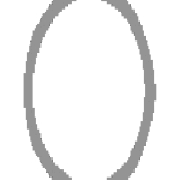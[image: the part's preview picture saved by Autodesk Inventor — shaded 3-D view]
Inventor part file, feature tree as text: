
AUTODESK INVENTOR PART (.ipt)
format: ipt  version: 2021 (Build 250183000, 183)  size: 113,152 bytes
history: native  units: in
note: dims shown in document units (in); Inventor stores cm internally (conversion verified against a paired STEP export)
features: other x4, sketch x3, plane x1
ambient origin geometry x8: Origin, YZ Plane, XZ Plane, XY Plane, X Axis, Y Axis, Z Axis, Center Point
bodies: Solid1 (feature_tree), Body (feature_tree)
feature tree (8):
  other  "Driven Length"
  other  "Frame Generator"
  other  "Start Plane"
  other  "End Plane"
  sketch  "Sketch"  dims[d2=10.9659in d4=-0.0in d5=10.9659in d6=0.12in d7=0.0in d8=90.0deg d9=10.9659in]
  sketch  "Sketch2"  dims[d0=1.0in]
  plane  "Work Plane3"
  sketch  "Sketch3"  dims[d1=0.065in]
